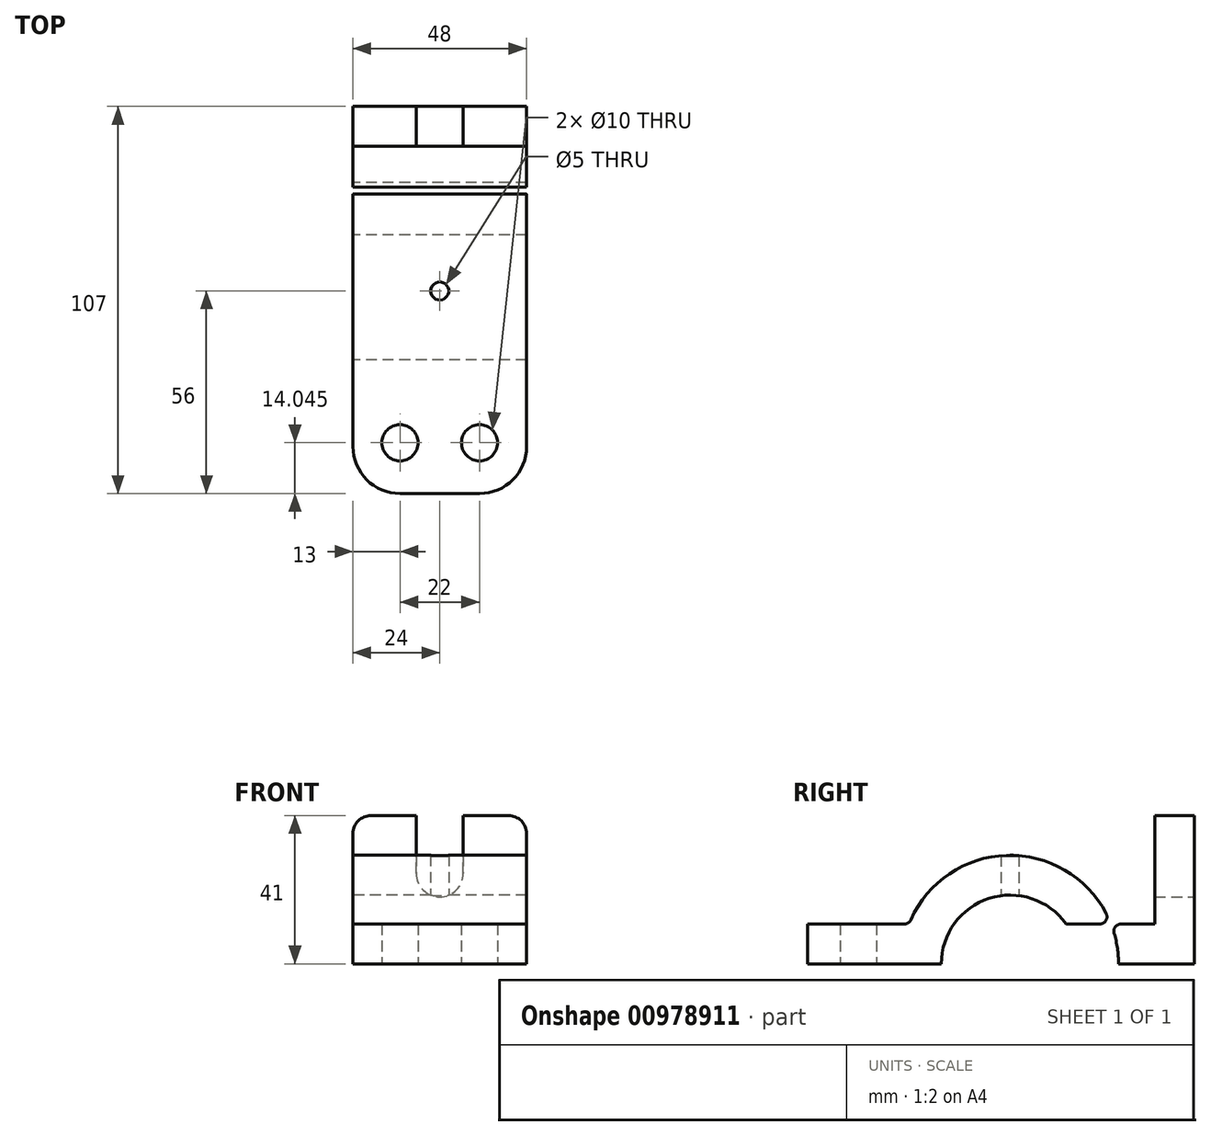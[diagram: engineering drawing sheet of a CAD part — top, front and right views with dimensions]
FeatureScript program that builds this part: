
annotation { "Feature Type Name" : "Feature", "Feature Type Description" : "" }
export const myFeature = defineFeature(function(context is Context, id is Id, definition is map)
    precondition{}
    {
        {
            var Q0;
            Q0=qCreatedBy(makeId("Right.planeOp"),FACE);
            var sketch = newSketch(context, id + "F0", { "sketchPlane" : qUnion([Q0])});
            skCircle(sketch, "E0", {"center": v(0, 0) * mm, "radius": 19 * mm});
            skCircle(sketch, "E1", {"center": v(0, 0) * mm, "radius": 30 * mm});
            skLineSegment(sketch, "E2.bottom", {"start": v(-56, 0) * mm, "end": v(51, 0) * mm});
            skLineSegment(sketch, "E2.top", {"start": v(-56, 11) * mm, "end": v(51, 11) * mm});
            skLineSegment(sketch, "E2.left", {"start": v(-56, 0) * mm, "end": v(-56, 11) * mm});
            skLineSegment(sketch, "E3", {"start": v(51, 0) * mm, "end": v(51, 41) * mm});
            skLineSegment(sketch, "E4", {"start": v(51, 41) * mm, "end": v(40, 41) * mm});
            skLineSegment(sketch, "E5", {"start": v(40, 41) * mm, "end": v(40, 11) * mm});
            skSolve(sketch);
        }
        {
            var Q0;
            {var subQ5=sQuery(id+"F0.wireOp",EDGE,"E2.left");Q0=makeQuery(id+"F0.imprint","IMPRINT",FACE,{"disambiguationData":[TD([[makeQuery(id+"F0.imprint","IMPRINT",EDGE,{"derivedFrom":subQ5}),-1.0]])]});}
            var Q1;
            {var subQ0=sQuery(id+"F0.wireOp",EDGE,"E2.top");var subQ1=sQuery(id+"F0.wireOp",EDGE,"E0");var subQ2=makeQuery(id+"F0.imprint","INTERSECT",VERTEX,{"disambiguationData":[OD(1.0)],"derivedFrom":[subQ1,subQ0]});Q1=makeQuery(id+"F0.imprint","IMPRINT",FACE,{"disambiguationData":[TD([[makeQuery(id+"F0.imprint","IMPRINT",EDGE,{"disambiguationData":[TD([[subQ2,-1.0]])],"derivedFrom":subQ1}),-1.0]])]});}
            var Q2;
            {var subQ0=sQuery(id+"F0.wireOp",EDGE,"E2.top");var subQ1=sQuery(id+"F0.wireOp",EDGE,"E0");var subQ2=makeQuery(id+"F0.imprint","INTERSECT",VERTEX,{"disambiguationData":[OD(0.0)],"derivedFrom":[subQ1,subQ0]});Q2=makeQuery(id+"F0.imprint","IMPRINT",FACE,{"disambiguationData":[TD([[makeQuery(id+"F0.imprint","IMPRINT",EDGE,{"disambiguationData":[TD([[subQ2,-1.0]])],"derivedFrom":subQ1}),-1.0]])]});}
            var Q3;
            {var subQ0=sQuery(id+"F0.wireOp",EDGE,"E2.top");var subQ1=sQuery(id+"F0.wireOp",EDGE,"E0");var subQ2=makeQuery(id+"F0.imprint","INTERSECT",VERTEX,{"disambiguationData":[OD(0.0)],"derivedFrom":[subQ1,subQ0]});Q3=makeQuery(id+"F0.imprint","IMPRINT",FACE,{"disambiguationData":[TD([[makeQuery(id+"F0.imprint","IMPRINT",EDGE,{"disambiguationData":[TD([[subQ2,1.0]])],"derivedFrom":subQ1}),-1.0]])]});}
            var Q4;
            {var subQ1=sQuery(id+"F0.wireOp",EDGE,"E2.top");var subQ4=sQuery(id+"F0.wireOp",EDGE,"E1");var subQ5=makeQuery(id+"F0.imprint","INTERSECT",VERTEX,{"disambiguationData":[OD(0.0)],"derivedFrom":[subQ4,subQ1]});Q4=makeQuery(id+"F0.imprint","IMPRINT",FACE,{"disambiguationData":[TD([[makeQuery(id+"F0.imprint","IMPRINT",EDGE,{"disambiguationData":[TD([[subQ5,1.0]])],"derivedFrom":subQ4}),-1.0]])]});}
            var Q5;
            {var subQ4=sQuery(id+"F0.wireOp",EDGE,"E4");Q5=makeQuery(id+"F0.imprint","IMPRINT",FACE,{"disambiguationData":[TD([[makeQuery(id+"F0.imprint","IMPRINT",EDGE,{"derivedFrom":subQ4}),1.0]])]});}
            extrude(context, id + "F1", {"entities" : qUnion([Q0, Q1, Q2, Q3, Q4, Q5]), "endBound" : BoundingType.SYMMETRIC, "depth" : 48 * mm, "offsetDistance" : 25 * mm});
        }
        {
            var Q0;
            Q0=makeQuery(id+"F1.opExtrude","SWEPT_FACE",FACE,{"disambiguationData":[OSD([sQuery(id+"F0.wireOp",EDGE,"E3")])]});
            var sketch = newSketch(context, id + "F2", { "sketchPlane" : qUnion([Q0])});
            skLineSegment(sketch, "E6", {"start": v(0, 41) * mm, "end": v(0, 0) * mm, "construction": true});
            skCircle(sketch, "E7", {"center": v(0, 25) * mm, "radius": 6.5 * mm});
            skLineSegment(sketch, "E8", {"start": v(-6.5, 25) * mm, "end": v(-6.5, 41) * mm});
            skLineSegment(sketch, "E9", {"start": v(6.5, 25) * mm, "end": v(6.5, 41) * mm});
            skSolve(sketch);
        }
        {
            var Q0;
            {var subQ0=sQuery(id+"F2.wireOp",EDGE,"E7");var subQ1=makeQuery(id+"F2.imprint","INTERSECT",VERTEX,{"derivedFrom":[subQ0,sQuery(id+"F2.wireOp",EDGE,"E8")]});Q0=makeQuery(id+"F2.imprint","IMPRINT",FACE,{"disambiguationData":[TD([[makeQuery(id+"F2.imprint","IMPRINT",EDGE,{"disambiguationData":[TD([[subQ1,1.0]])],"derivedFrom":subQ0}),1.0]])]});}
            var Q1;
            {var subQ0=sQuery(id+"F2.wireOp",EDGE,"E8");Q1=makeQuery(id+"F2.imprint","IMPRINT",FACE,{"disambiguationData":[TD([[makeQuery(id+"F2.imprint","IMPRINT",EDGE,{"derivedFrom":subQ0}),-1.0]])]});}
            var Q2;
            Q2=makeQuery(id+"F1.opExtrude","SWEPT_FACE",FACE,{"disambiguationData":[OSD([sQuery(id+"F0.wireOp",EDGE,"E5")])]});
            extrude(context, id + "F3", {"entities" : qUnion([Q0, Q1]), "operationType" : NewBodyOperationType.REMOVE, "endBound" : BoundingType.UP_TO_SURFACE, "oppositeDirection" : true, "depth" : 25 * mm, "endBoundEntityFace" : qUnion([Q2]), "offsetDistance" : 25 * mm});
        }
        {
            var Q0;
            Q0=qCreatedBy(makeId("Top.planeOp"),FACE);
            var sketch = newSketch(context, id + "F4", { "sketchPlane" : qUnion([Q0])});
            skCircle(sketch, "E10", {"center": v(0, 0) * mm, "radius": 2.5 * mm});
            skLineSegment(sketch, "E11", {"start": v(0, -56) * mm, "end": v(0, -27.91) * mm, "construction": true});
            skLineSegment(sketch, "E12", {"start": v(-24, -41.96) * mm, "end": v(24, -41.96) * mm, "construction": true});
            skPoint(sketch, "E12.startSnap0", {"position": v(0, -41.96) * mm});
            skCircle(sketch, "E13", {"center": v(-11, -41.96) * mm, "radius": 5 * mm});
            skCircle(sketch, "E14", {"center": v(11, -41.96) * mm, "radius": 5 * mm});
            skSolve(sketch);
        }
        {
            var Q0;
            Q0=makeQuery(id+"F4.imprint","IMPRINT",FACE,{"disambiguationData":[TD([[makeQuery(id+"F4.imprint","IMPRINT",EDGE,{"derivedFrom":sQuery(id+"F4.wireOp",EDGE,"E14")}),1.0]])]});
            var Q1;
            Q1=makeQuery(id+"F4.imprint","IMPRINT",FACE,{"disambiguationData":[TD([[makeQuery(id+"F4.imprint","IMPRINT",EDGE,{"derivedFrom":sQuery(id+"F4.wireOp",EDGE,"E13")}),1.0]])]});
            var Q2;
            Q2=makeQuery(id+"F4.imprint","IMPRINT",FACE,{"disambiguationData":[TD([[makeQuery(id+"F4.imprint","IMPRINT",EDGE,{"derivedFrom":sQuery(id+"F4.wireOp",EDGE,"E10")}),1.0]])]});
            extrude(context, id + "F5", {"entities" : qUnion([Q0, Q1, Q2]), "operationType" : NewBodyOperationType.REMOVE, "endBound" : BoundingType.THROUGH_ALL, "depth" : 25 * mm, "offsetDistance" : 25 * mm});
        }
        {
            var Q0;
            Q0=makeQuery(id+"F1.opExtrude","CAP_EDGE",EDGE,{"disambiguationData":[OSD([sQuery(id+"F0.wireOp",EDGE,"E4")])],"isStart":false});
            var Q1;
            Q1=makeQuery(id+"F1.opExtrude","CAP_EDGE",EDGE,{"disambiguationData":[OSD([sQuery(id+"F0.wireOp",EDGE,"E4")])],"isStart":true});
            fillet(context, id + "F6", {"entities" : qUnion([Q0, Q1]), "radius" : 5 * mm, "tangentPropagation" : true, "allowEdgeOverflow" : false});
        }
        {
            var Q0;
            Q0=makeQuery(id+"F1.opExtrude","CAP_EDGE",EDGE,{"disambiguationData":[OSD([sQuery(id+"F0.wireOp",EDGE,"E2.left")])],"isStart":false});
            var Q1;
            Q1=makeQuery(id+"F1.opExtrude","CAP_EDGE",EDGE,{"disambiguationData":[OSD([sQuery(id+"F0.wireOp",EDGE,"E2.left")])],"isStart":true});
            fillet(context, id + "F7", {"entities" : qUnion([Q0, Q1]), "radius" : 13 * mm, "tangentPropagation" : true, "allowEdgeOverflow" : false});
        }
        {
            var Q0;
            {var subQ0=sQuery(id+"F0.wireOp",EDGE,"E2.top");var subQ1=sQuery(id+"F0.wireOp",EDGE,"E1");Q0=makeQuery(id+"F1.opExtrude","SWEPT_EDGE",EDGE,{"disambiguationData":[OSD([subQ1,subQ0]),TDD([makeQuery(id+"F0.imprint","INTERSECT",VERTEX,{"disambiguationData":[OD(1.0)],"derivedFrom":[subQ1,subQ0]})])]});}
            var Q1;
            {var subQ0=sQuery(id+"F0.wireOp",EDGE,"E2.top");var subQ1=sQuery(id+"F0.wireOp",EDGE,"E1");Q1=makeQuery(id+"F1.opExtrude","SWEPT_EDGE",EDGE,{"disambiguationData":[OSD([subQ1,subQ0]),TDD([makeQuery(id+"F0.imprint","INTERSECT",VERTEX,{"disambiguationData":[OD(0.0)],"derivedFrom":[subQ1,subQ0]})])]});}
            fillet(context, id + "F8", {"entities" : qUnion([Q0, Q1]), "radius" : 2 * mm, "tangentPropagation" : true, "allowEdgeOverflow" : false});
        }
    });
